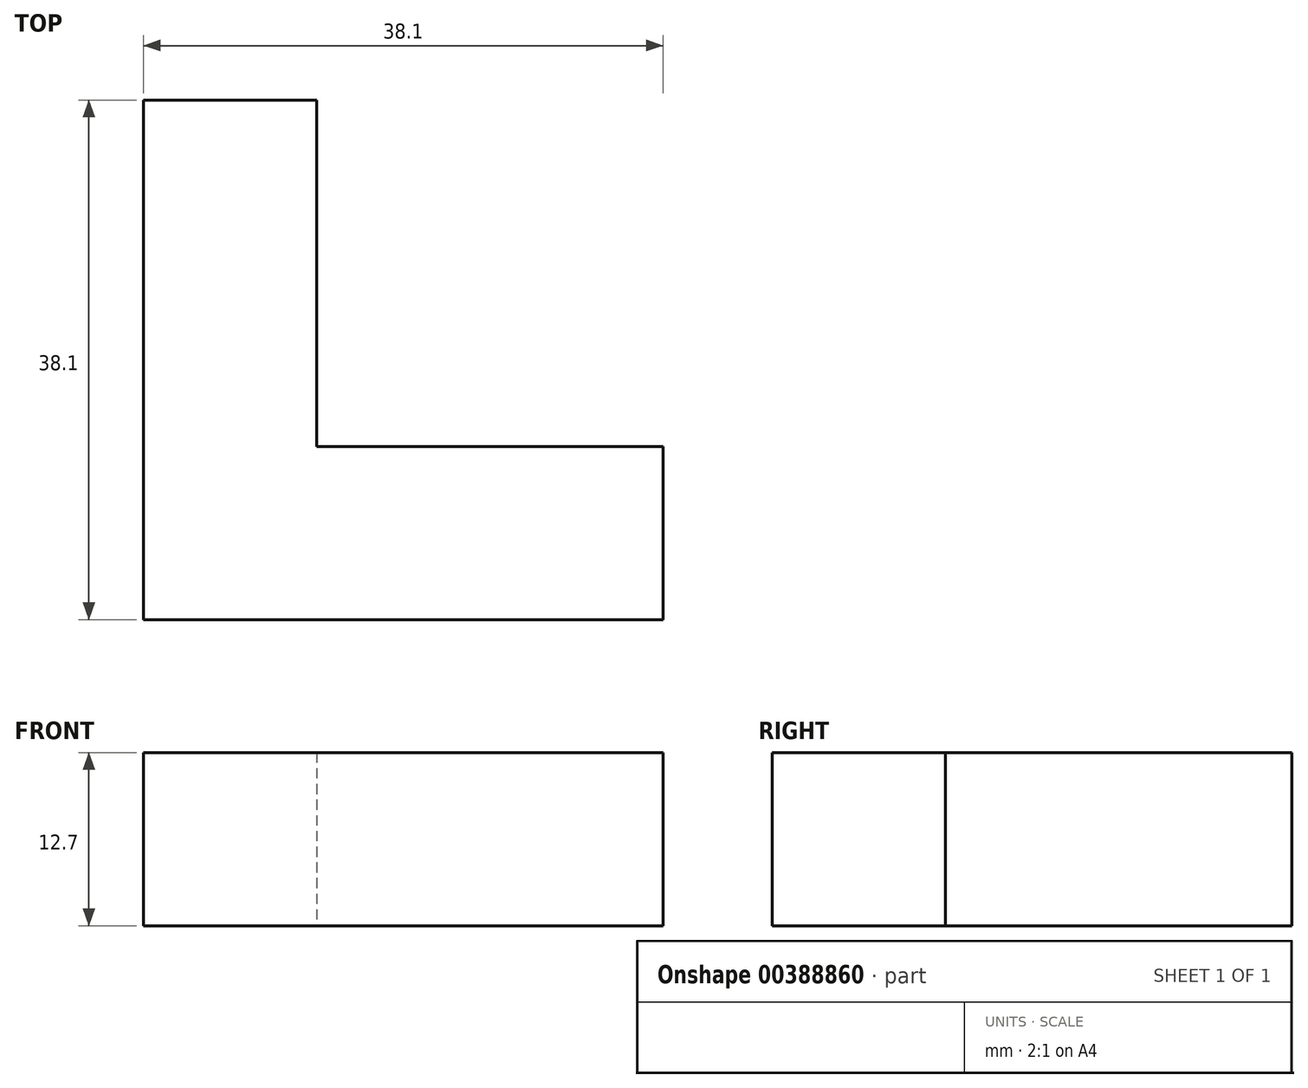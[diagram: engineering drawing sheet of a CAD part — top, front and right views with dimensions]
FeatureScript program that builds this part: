
annotation { "Feature Type Name" : "Feature", "Feature Type Description" : "" }
export const myFeature = defineFeature(function(context is Context, id is Id, definition is map)
    precondition{}
    {
        {
            var Q0;
            Q0=qCreatedBy(makeId("Top.planeOp"),FACE);
            var sketch = newSketch(context, id + "F0", { "sketchPlane" : qUnion([Q0])});
            skLineSegment(sketch, "E0.bottom", {"start": v(0, 0) * mm, "end": v(38.1, 0) * mm});
            skLineSegment(sketch, "E0.left", {"start": v(0, 0) * mm, "end": v(0, 12.7) * mm});
            skLineSegment(sketch, "E0.right", {"start": v(38.1, 0) * mm, "end": v(38.1, 12.7) * mm});
            skLineSegment(sketch, "E1.top", {"start": v(0, 38.1) * mm, "end": v(12.7, 38.1) * mm});
            skLineSegment(sketch, "E1.left", {"start": v(0, 12.7) * mm, "end": v(0, 38.1) * mm});
            skLineSegment(sketch, "E1.right", {"start": v(12.7, 12.7) * mm, "end": v(12.7, 38.1) * mm});
            skLineSegment(sketch, "E2", {"start": v(12.7, 12.7) * mm, "end": v(38.1, 12.7) * mm});
            skSolve(sketch);
        }
        {
            var Q0;
            Q0=makeQuery(id+"F0.imprint","IMPRINT",FACE,{"disambiguationData":[TD([[makeQuery(id+"F0.imprint","IMPRINT",EDGE,{"derivedFrom":sQuery(id+"F0.wireOp",EDGE,"E0.bottom")}),1.0]])]});
            extrude(context, id + "F1", {"entities" : qUnion([Q0]), "depth" : 12.7 * mm});
        }
    });
